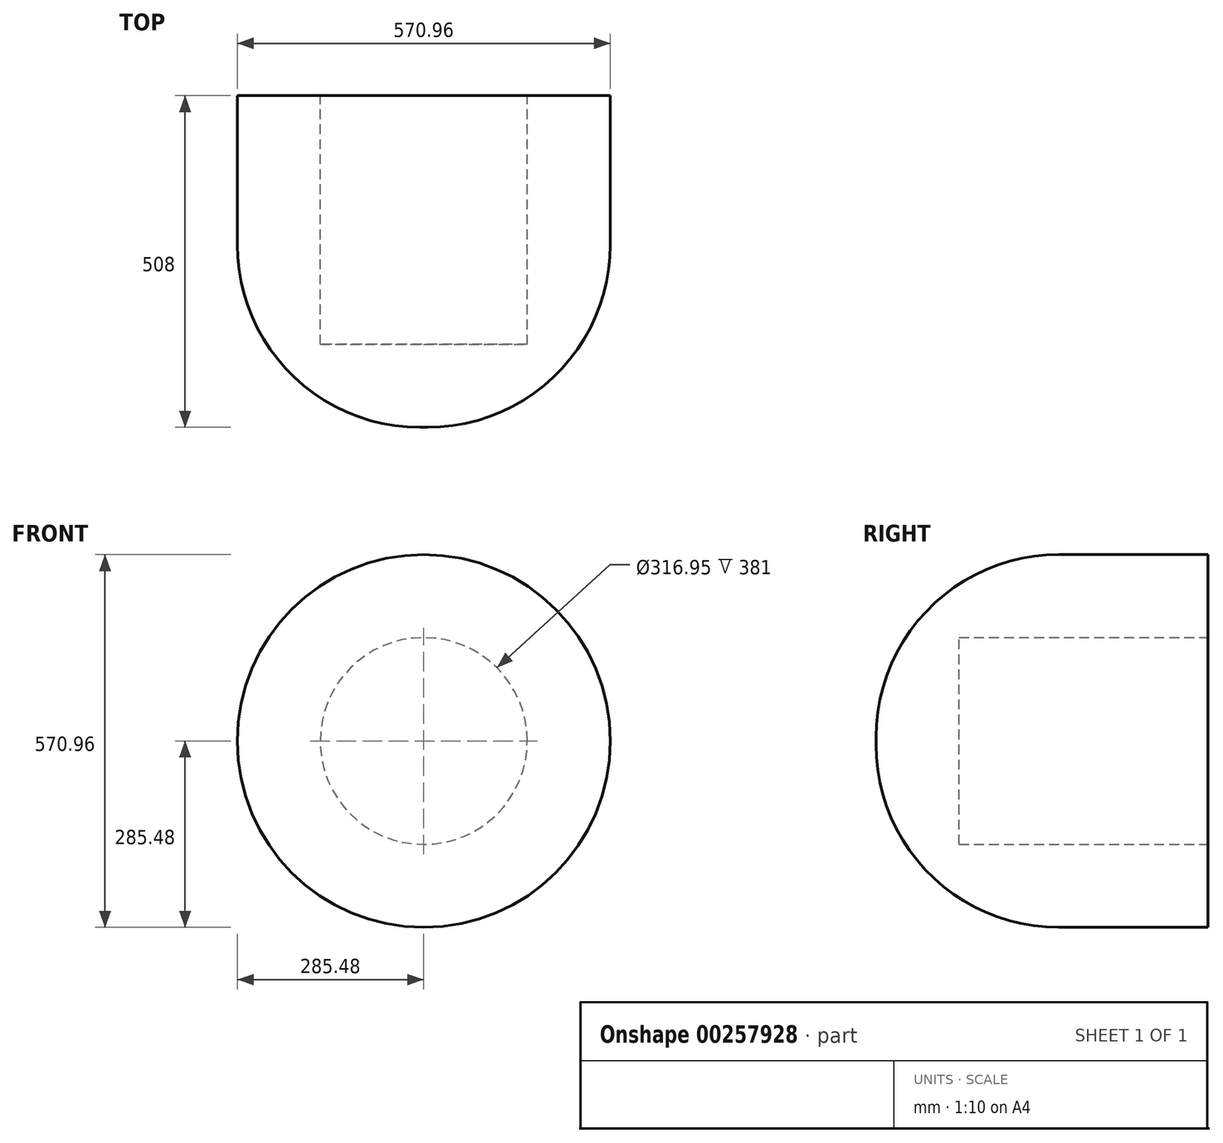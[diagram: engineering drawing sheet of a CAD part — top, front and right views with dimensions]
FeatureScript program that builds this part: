
annotation { "Feature Type Name" : "Feature", "Feature Type Description" : "" }
export const myFeature = defineFeature(function(context is Context, id is Id, definition is map)
    precondition{}
    {
        {
            var Q0;
            Q0=qCreatedBy(makeId("Front.planeOp"),FACE);
            var sketch = newSketch(context, id + "F0", { "sketchPlane" : qUnion([Q0])});
            skCircle(sketch, "E0", {"center": v(0, 0) * mm, "radius": 285.48 * mm});
            skSolve(sketch);
        }
        {
            var Q0;
            Q0=makeQuery(id+"F0.imprint","IMPRINT",FACE,{"disambiguationData":[TD([[makeQuery(id+"F0.imprint","IMPRINT",EDGE,{"derivedFrom":sQuery(id+"F0.wireOp",EDGE,"E0")}),1.0]])]});
            extrude(context, id + "F1", {"entities" : qUnion([Q0]), "depth" : 508 * mm});
        }
        {
            var Q0;
            Q0=makeQuery(id+"F1.opExtrude","CAP_FACE",FACE,{"disambiguationData":[OSD([sQuery(id+"F0.wireOp",EDGE,"E0")])],"isStart":true});
            shell(context, id + "F2", {"entities" : qUnion([Q0]), "thickness" : 127 * mm});
        }
        {
            var Q0;
            Q0=makeQuery(id+"F1.opExtrude","CAP_EDGE",EDGE,{"disambiguationData":[OSD([sQuery(id+"F0.wireOp",EDGE,"E0")])],"isStart":false});
            fillet(context, id + "F3", {"entities" : qUnion([Q0]), "radius" : 279.4 * mm, "tangentPropagation" : true, "allowEdgeOverflow" : false});
        }
    });
